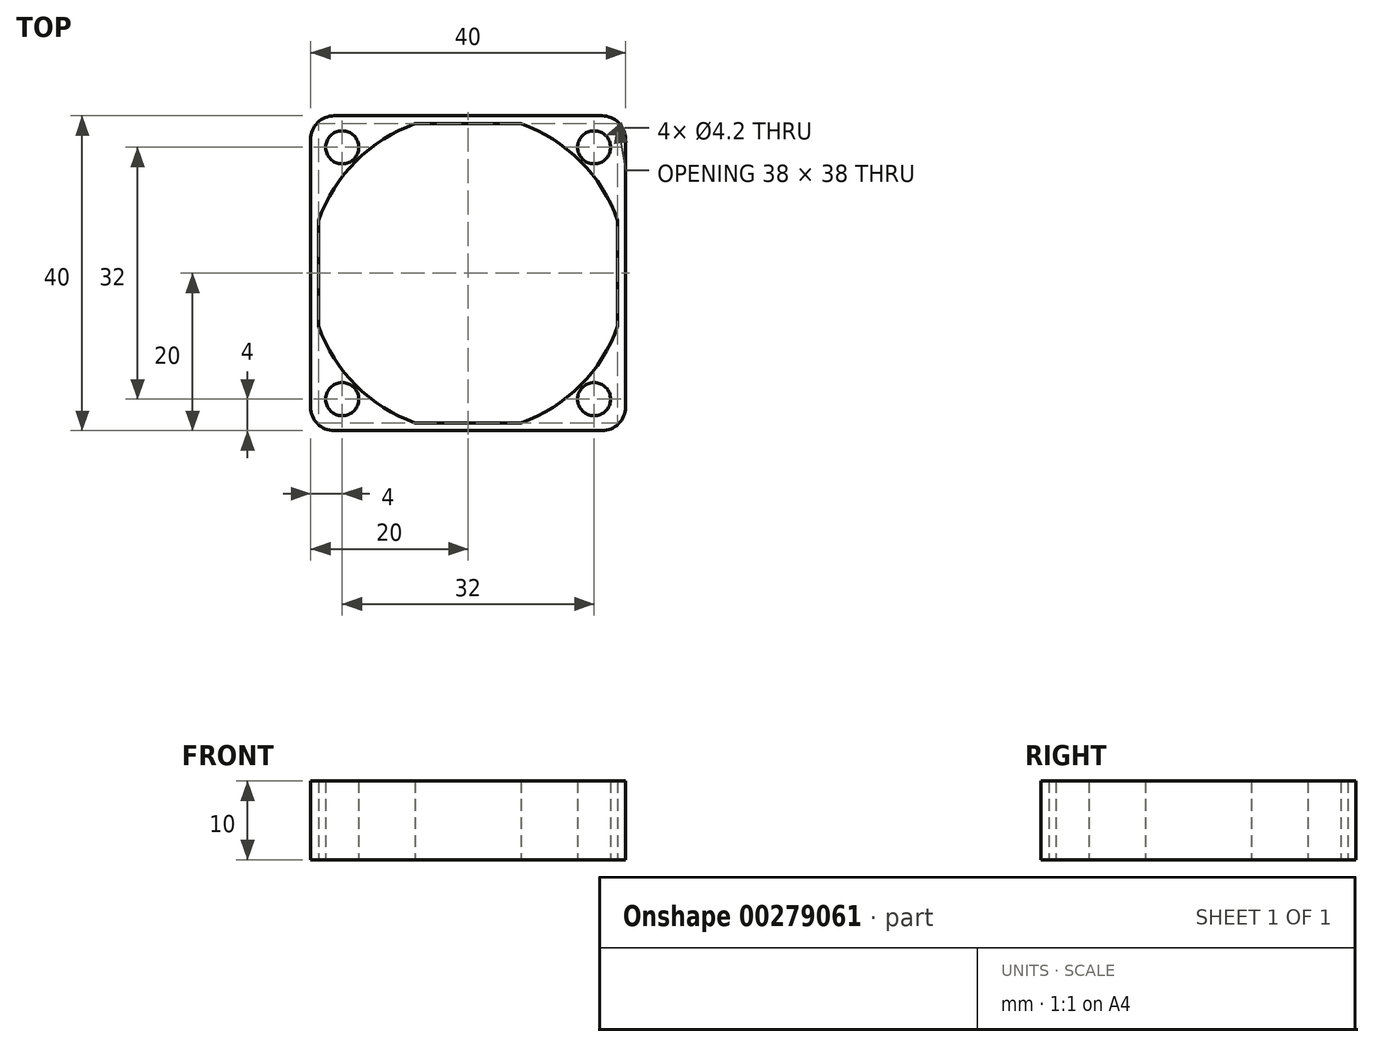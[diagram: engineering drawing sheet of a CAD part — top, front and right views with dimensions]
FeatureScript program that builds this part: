
annotation { "Feature Type Name" : "Feature", "Feature Type Description" : "" }
export const myFeature = defineFeature(function(context is Context, id is Id, definition is map)
    precondition{}
    {
        {
            var Q0;
            Q0=qCreatedBy(makeId("Top.planeOp"),FACE);
            var sketch = newSketch(context, id + "F0", { "sketchPlane" : qUnion([Q0])});
            skLineSegment(sketch, "E0.bottom", {"start": v(-17, 20) * mm, "end": v(17, 20) * mm});
            skLineSegment(sketch, "E0.top", {"start": v(-17, -20) * mm, "end": v(17, -20) * mm});
            skLineSegment(sketch, "E0.left", {"start": v(-20, 17) * mm, "end": v(-20, -17) * mm});
            skLineSegment(sketch, "E0.right", {"start": v(20, 17) * mm, "end": v(20, -17) * mm});
            skPoint(sketch, "E0.middle", {"position": v(0, 0) * mm});
            skLineSegment(sketch, "E1.bottom", {"start": v(-16, 16) * mm, "end": v(16, 16) * mm, "construction": true});
            skLineSegment(sketch, "E1.top", {"start": v(-16, -16) * mm, "end": v(16, -16) * mm, "construction": true});
            skLineSegment(sketch, "E1.left", {"start": v(-16, 16) * mm, "end": v(-16, -16) * mm, "construction": true});
            skLineSegment(sketch, "E1.right", {"start": v(16, 16) * mm, "end": v(16, -16) * mm, "construction": true});
            skCircle(sketch, "E2", {"center": v(-16, 16) * mm, "radius": 2.1 * mm});
            skCircle(sketch, "E3.1.0", {"center": v(-16, -16) * mm, "radius": 2.1 * mm});
            skCircle(sketch, "E3.2.0", {"center": v(16, -16) * mm, "radius": 2.1 * mm});
            skCircle(sketch, "E3.3.0", {"center": v(16, 16) * mm, "radius": 2.1 * mm});
            skArc(sketch, "E4", {"start": v(-6.7, 19) * mm, "mid": v(-14.25, 14.25) * mm, "end": v(-19, 6.7) * mm});
            skArc(sketch, "E5.1.0", {"start": v(-19, -6.7) * mm, "mid": v(-14.25, -14.25) * mm, "end": v(-6.7, -19) * mm});
            skArc(sketch, "E5.2.0", {"start": v(6.7, -19) * mm, "mid": v(14.25, -14.25) * mm, "end": v(19, -6.7) * mm});
            skArc(sketch, "E5.3.0", {"start": v(19, 6.7) * mm, "mid": v(14.25, 14.25) * mm, "end": v(6.7, 19) * mm});
            skLineSegment(sketch, "E6", {"start": v(-19, 6.7) * mm, "end": v(-19, -6.7) * mm});
            skLineSegment(sketch, "E7", {"start": v(-6.7, -19) * mm, "end": v(6.7, -19) * mm});
            skLineSegment(sketch, "E8", {"start": v(19, -6.7) * mm, "end": v(19, 6.7) * mm});
            skLineSegment(sketch, "E9", {"start": v(6.7, 19) * mm, "end": v(-6.7, 19) * mm});
            skPoint(sketch, "E10.visualSharp", {"position": v(-20, 20) * mm});
            skArc(sketch, "E10.filletArc", {"start": v(-17, 20) * mm, "mid": v(-19.12, 19.12) * mm, "end": v(-20, 17) * mm});
            skPoint(sketch, "E11.visualSharp", {"position": v(20, 20) * mm});
            skArc(sketch, "E11.filletArc", {"start": v(20, 17) * mm, "mid": v(19.12, 19.12) * mm, "end": v(17, 20) * mm});
            skPoint(sketch, "E12.visualSharp", {"position": v(20, -20) * mm});
            skArc(sketch, "E12.filletArc", {"start": v(17, -20) * mm, "mid": v(19.12, -19.12) * mm, "end": v(20, -17) * mm});
            skPoint(sketch, "E13.visualSharp", {"position": v(-20, -20) * mm});
            skArc(sketch, "E13.filletArc", {"start": v(-20, -17) * mm, "mid": v(-19.12, -19.12) * mm, "end": v(-17, -20) * mm});
            skSolve(sketch);
        }
        {
            var Q0;
            Q0 = qSketchRegion(id + "F0", true);
            extrude(context, id + "F1", {"entities" : qUnion([Q0]), "depth" : 10 * mm});
        }
    });
